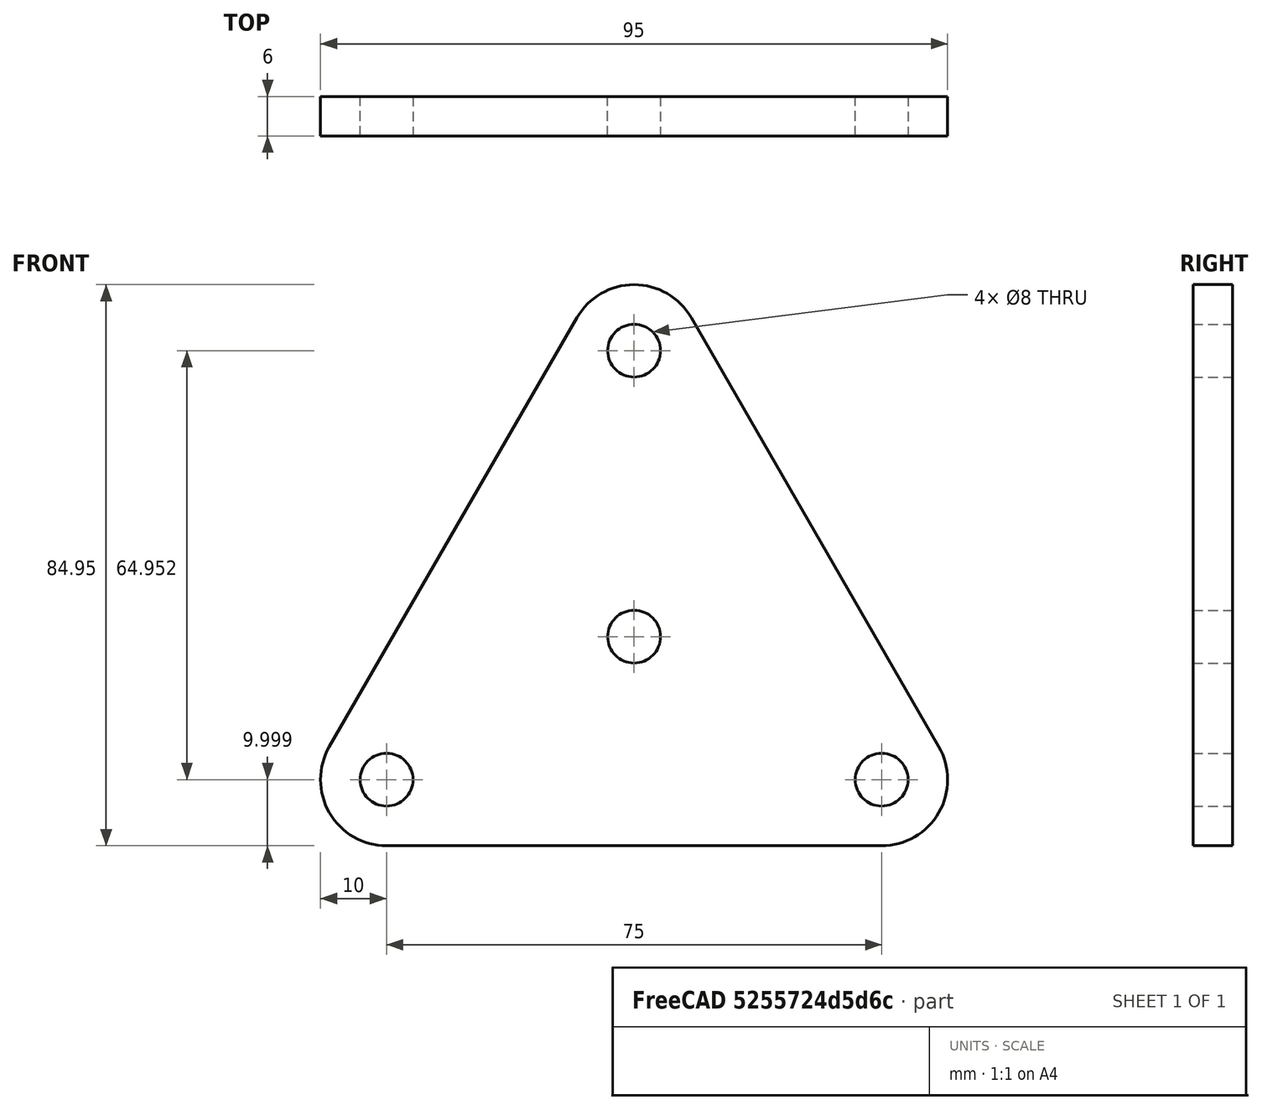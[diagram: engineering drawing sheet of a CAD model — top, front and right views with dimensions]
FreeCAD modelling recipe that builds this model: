
FCSTD DOCUMENT  (FreeCAD 0.18R16117 (Git))
Label: 90cm_dish_mount_adapter
License: All rights reserved
LicenseURL: http://en.wikipedia.org/wiki/All_rights_reserved
objects: Sketcher::SketchObject×1, PartDesign::Pad×1, PartDesign::Body×1
note: 4 computed .brp shape members not serialized (recipe doc carries the construction recipe); baked Part::Feature solids carry a one-line shape summary decoded from their .brp

FEATURE [Sketcher::SketchObject] Sketch
  MapMode = 5
  Placement = pos=(0,0,0) rot=(1,0,0;1.5708rad)
  Support = -> [XZ_Plane]
  expr: Constraints[31] = Sketch.Constraints.screw_hole_size + 6mm
  expr: Constraints[32] = Sketch.Constraints.screw_hole_size
  expr: Constraints[4] = Sketch.Constraints.screw_hole_dist
  expr: Constraints[5] = Sketch.Constraints.screw_hole_dist
  expr: Constraints[2] = Sketch.Constraints.screw_hole_size
  sketch-geometry (16):
    g0: Circle CenterX=7.1e-15 CenterY=43.3013 CenterZ=0 NormalX=0 NormalY=0 NormalZ=1 AngleXU=0 Radius=4
    g1: Circle CenterX=37.5 CenterY=-21.6506 CenterZ=0 NormalX=0 NormalY=0 NormalZ=1 AngleXU=0 Radius=4
    g2: Circle CenterX=-37.5 CenterY=-21.6506 CenterZ=0 NormalX=0 NormalY=0 NormalZ=1 AngleXU=0 Radius=4
    g3: LineSegment [constr] StartX=37.5 StartY=-21.6506 StartZ=0 EndX=-58.3486 EndY=33.6876 EndZ=0
    g4: LineSegment [constr] StartX=-37.5 StartY=-21.6506 StartZ=0 EndX=7.1e-15 EndY=43.3013 EndZ=0
    g5: LineSegment [constr] StartX=7.1e-15 StartY=43.3013 StartZ=0 EndX=37.5 EndY=-21.6506 EndZ=0
    g6: LineSegment [constr] StartX=-37.5 StartY=-21.6506 StartZ=0 EndX=37.5 EndY=-21.6506 EndZ=0
    g7: LineSegment [constr] StartX=-37.5 StartY=-21.6506 StartZ=0 EndX=54.011 EndY=31.1833 EndZ=0
    g8: LineSegment [constr] StartX=7.1e-15 StartY=43.3013 StartZ=0 EndX=7.1e-15 EndY=-67.8684 EndZ=0
    g9: LineSegment StartX=46.1603 StartY=-16.6506 StartZ=0 EndX=8.66032 EndY=48.3013 EndZ=0
    g10: LineSegment StartX=-8.66032 StartY=48.3013 StartZ=0 EndX=-46.1603 EndY=-16.6506 EndZ=0
    g11: LineSegment StartX=-37.5 StartY=-31.6506 StartZ=0 EndX=37.5 EndY=-31.6506 EndZ=0
    g12: ArcOfCircle CenterX=7.1e-15 CenterY=43.3013 CenterZ=0 NormalX=0 NormalY=0 NormalZ=1 AngleXU=0 Radius=10.0001 StartAngle=0.523598 EndAngle=2.61799
    g13: ArcOfCircle CenterX=-37.5 CenterY=-21.6506 CenterZ=0 NormalX=0 NormalY=0 NormalZ=1 AngleXU=0 Radius=10 StartAngle=2.61799 EndAngle=4.71239
    g14: ArcOfCircle CenterX=37.5 CenterY=-21.6506 CenterZ=0 NormalX=0 NormalY=0 NormalZ=1 AngleXU=0 Radius=10 StartAngle=4.71239 EndAngle=6.80678
    g15: Circle CenterX=0 CenterY=0 CenterZ=0 NormalX=0 NormalY=0 NormalZ=1 AngleXU=0 Radius=4
  constraints (33):
    c: Radius(g0) = 4  'screw_hole_size'
    c: Radius(g1) = 4
    c: Radius(g2) = 4
    c: Distance(g0,g1) = 75  'screw_hole_dist'
    c: Distance(g2,g1) = 75
    c: Distance(g2,g0) = 75
    c: Symmetric(g1,g2,g-2)
    c: Coincident(g4,g2)
    c: Coincident(g4,g0)
    c: Coincident(g3,g1)
    c: Perpendicular(g3,g4)
    c: PointOnObject(g-1,g3)
    c: Coincident(g8,g0)
    c: Perpendicular(g6,g8)
    c: Coincident(g6,g2)
    c: Coincident(g6,g1)
    c: Perpendicular(g7,g5)
    c: Coincident(g7,g2)
    c: Coincident(g5,g0)
    c: Coincident(g5,g1)
    c: Equal(g9,g10)
    c: Equal(g9,g11)
    c: Tangent(g9,g12) = -1.5708
    c: Tangent(g10,g12) = -1.5708
    c: Tangent(g10,g13) = -1.5708
    c: Tangent(g11,g13) = -1.5708
    c: Tangent(g9,g14) = -1.5708
    c: Tangent(g11,g14) = -1.5708
    c: Coincident(g14,g1)
    c: Coincident(g2,g13)
    c: Coincident(g12,g0)
    c: Distance(g11,g1) = 10
    c: Radius(g15) = 4
FEATURE [PartDesign::Pad] Pad
  Length = 6
  Length2 = 100
  Placement = pos=(0,0,0) rot=(1,0,0;1.5708rad)
  Profile = -> Sketch
  Type = 0
FEATURE [PartDesign::Body] Body
  Group = -> [Sketch,Pad]
  Origin = -> Origin
  Tip = -> Pad
